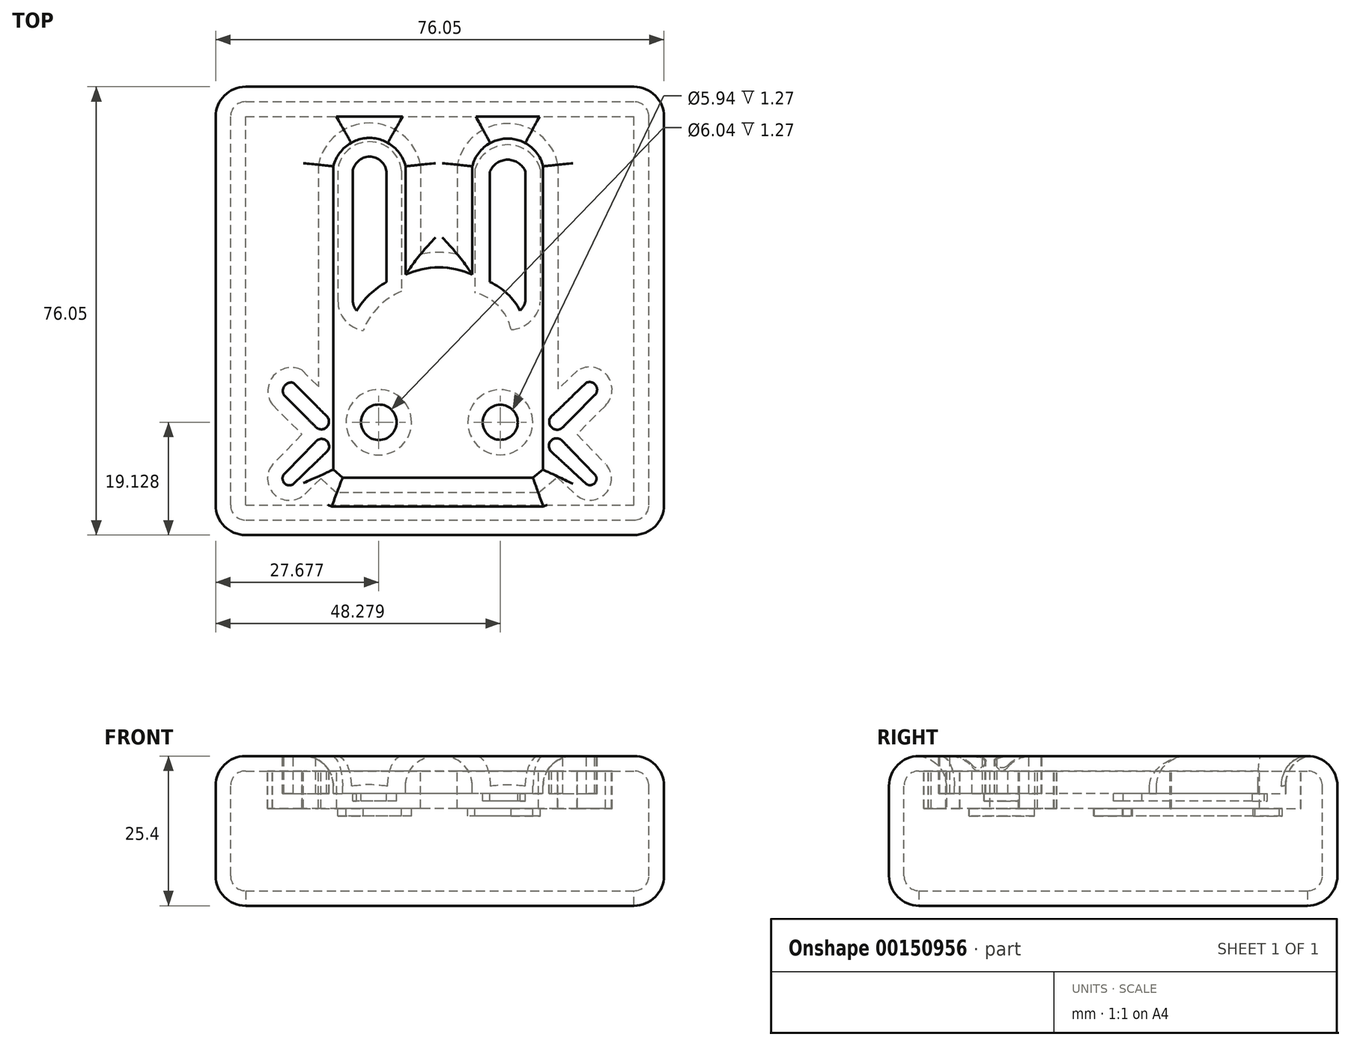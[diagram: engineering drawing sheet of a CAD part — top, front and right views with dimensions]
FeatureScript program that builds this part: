
annotation { "Feature Type Name" : "Feature", "Feature Type Description" : "" }
export const myFeature = defineFeature(function(context is Context, id is Id, definition is map)
    precondition{}
    {
        {
            var Q0;
            Q0=qCreatedBy(makeId("Top.planeOp"),FACE);
            var sketch = newSketch(context, id + "F0", { "sketchPlane" : qUnion([Q0])});
            skLineSegment(sketch, "E0.bottom", {"start": v(0, 0) * mm, "end": v(76.05, 0) * mm});
            skLineSegment(sketch, "E0.top", {"start": v(0, 76.05) * mm, "end": v(76.05, 76.05) * mm});
            skLineSegment(sketch, "E0.left", {"start": v(0, 0) * mm, "end": v(0, 76.05) * mm});
            skLineSegment(sketch, "E0.right", {"start": v(76.05, 0) * mm, "end": v(76.05, 76.05) * mm});
            skSolve(sketch);
        }
        {
            var Q0;
            Q0 = qSketchRegion(id + "F0", true);
            extrude(context, id + "F1", {"entities" : qUnion([Q0]), "depth" : 25.4 * mm});
        }
        {
            var Q0;
            Q0=makeQuery(id+"F1.opExtrude","CAP_FACE",FACE,{"disambiguationData":[OSD([sQuery(id+"F0.wireOp",EDGE,"E0.bottom"),sQuery(id+"F0.wireOp",EDGE,"E0.top"),sQuery(id+"F0.wireOp",EDGE,"E0.left"),sQuery(id+"F0.wireOp",EDGE,"E0.right")])],"isStart":false});
            var sketch = newSketch(context, id + "F2", { "sketchPlane" : qUnion([Q0])});
            skPoint(sketch, "E1", {"position": v(11.59, 23.74) * mm});
            skPoint(sketch, "E2", {"position": v(11.59, 10.3) * mm});
            skPoint(sketch, "E3", {"position": v(13.2, 8.63) * mm});
            skPoint(sketch, "E4", {"position": v(13.2, 25.84) * mm});
            skPoint(sketch, "E5", {"position": v(64.31, 23.74) * mm});
            skPoint(sketch, "E6", {"position": v(64.31, 10.3) * mm});
            skPoint(sketch, "E7", {"position": v(62.9, 25.84) * mm});
            skPoint(sketch, "E8", {"position": v(62.9, 8.63) * mm});
            skPoint(sketch, "E9", {"position": v(17.01, 15.85) * mm});
            skPoint(sketch, "E10", {"position": v(17.01, 18.3) * mm});
            skPoint(sketch, "E11", {"position": v(18.82, 20.17) * mm});
            skPoint(sketch, "E12", {"position": v(18.82, 14.1) * mm});
            skPoint(sketch, "E13", {"position": v(58.92, 15.85) * mm});
            skPoint(sketch, "E14", {"position": v(58.92, 18.3) * mm});
            skPoint(sketch, "E15", {"position": v(57, 20.17) * mm});
            skPoint(sketch, "E16", {"position": v(57, 14.1) * mm});
            skPoint(sketch, "E17", {"position": v(27.68, 19.13) * mm});
            skPoint(sketch, "E18", {"position": v(48.28, 19.13) * mm});
            skCircle(sketch, "E19", {"center": v(27.68, 19.13) * mm, "radius": 3.02 * mm});
            skCircle(sketch, "E20", {"center": v(48.28, 19.13) * mm, "radius": 2.97 * mm});
            skArc(sketch, "E21", {"start": v(13.2, 25.84) * mm, "mid": v(11.7, 25.31) * mm, "end": v(11.59, 23.74) * mm});
            skArc(sketch, "E22", {"start": v(17.01, 18.3) * mm, "mid": v(18.86, 18.32) * mm, "end": v(18.82, 20.17) * mm});
            skArc(sketch, "E23", {"start": v(18.82, 14.1) * mm, "mid": v(18.86, 15.95) * mm, "end": v(17.01, 15.85) * mm});
            skArc(sketch, "E24", {"start": v(11.59, 10.3) * mm, "mid": v(11.68, 8.78) * mm, "end": v(13.2, 8.63) * mm});
            skArc(sketch, "E25", {"start": v(57, 20.17) * mm, "mid": v(57, 18.25) * mm, "end": v(58.92, 18.3) * mm});
            skArc(sketch, "E26", {"start": v(64.31, 23.74) * mm, "mid": v(64.5, 25.38) * mm, "end": v(62.9, 25.84) * mm});
            skArc(sketch, "E27", {"start": v(58.92, 15.85) * mm, "mid": v(56.96, 16.07) * mm, "end": v(57, 14.1) * mm});
            skArc(sketch, "E28", {"start": v(62.9, 8.63) * mm, "mid": v(64.34, 8.85) * mm, "end": v(64.31, 10.3) * mm});
            skLineSegment(sketch, "E29", {"start": v(13.2, 25.84) * mm, "end": v(18.82, 20.17) * mm});
            skLineSegment(sketch, "E30", {"start": v(11.59, 23.74) * mm, "end": v(17.01, 18.3) * mm});
            skLineSegment(sketch, "E31", {"start": v(17.01, 15.85) * mm, "end": v(11.59, 10.3) * mm});
            skLineSegment(sketch, "E32", {"start": v(18.82, 14.1) * mm, "end": v(13.2, 8.63) * mm});
            skLineSegment(sketch, "E33", {"start": v(57, 14.1) * mm, "end": v(62.9, 8.63) * mm});
            skLineSegment(sketch, "E34", {"start": v(58.92, 15.85) * mm, "end": v(64.31, 10.3) * mm});
            skLineSegment(sketch, "E35", {"start": v(64.31, 23.74) * mm, "end": v(58.92, 18.3) * mm});
            skLineSegment(sketch, "E36", {"start": v(62.9, 25.84) * mm, "end": v(57, 20.17) * mm});
            skPoint(sketch, "E37", {"position": v(23.24, 61.64) * mm});
            skPoint(sketch, "E38", {"position": v(29, 61.64) * mm});
            skPoint(sketch, "E39", {"position": v(46.53, 61.64) * mm});
            skPoint(sketch, "E40", {"position": v(52.56, 61.64) * mm});
            skPoint(sketch, "E41", {"position": v(52.56, 39.74) * mm});
            skPoint(sketch, "E42", {"position": v(51.63, 38.07) * mm});
            skPoint(sketch, "E43", {"position": v(23.89, 38.07) * mm});
            skPoint(sketch, "E44", {"position": v(23.28, 39.74) * mm});
            skPoint(sketch, "E45", {"position": v(29, 42.91) * mm});
            skPoint(sketch, "E46", {"position": v(46.53, 42.91) * mm});
            skArc(sketch, "E47", {"start": v(29, 61.64) * mm, "mid": v(26.12, 64.18) * mm, "end": v(23.24, 61.64) * mm});
            skArc(sketch, "E48", {"start": v(52.56, 61.64) * mm, "mid": v(49.54, 63.67) * mm, "end": v(46.53, 61.64) * mm});
            skArc(sketch, "E49", {"start": v(51.63, 38.07) * mm, "mid": v(49.5, 40.93) * mm, "end": v(46.53, 42.91) * mm});
            skArc(sketch, "E50", {"start": v(29, 42.91) * mm, "mid": v(26.14, 40.81) * mm, "end": v(23.89, 38.07) * mm});
            skArc(sketch, "E51", {"start": v(23.28, 39.74) * mm, "mid": v(23.43, 38.85) * mm, "end": v(23.89, 38.07) * mm});
            skArc(sketch, "E52", {"start": v(51.63, 38.07) * mm, "mid": v(52.24, 38.82) * mm, "end": v(52.56, 39.74) * mm});
            skLineSegment(sketch, "E53", {"start": v(23.24, 61.64) * mm, "end": v(23.28, 39.74) * mm});
            skLineSegment(sketch, "E54", {"start": v(29, 61.64) * mm, "end": v(29, 42.91) * mm});
            skLineSegment(sketch, "E55", {"start": v(46.53, 61.64) * mm, "end": v(46.53, 42.91) * mm});
            skLineSegment(sketch, "E56", {"start": v(52.56, 61.64) * mm, "end": v(52.56, 39.74) * mm});
            skPoint(sketch, "E57", {"position": v(19.97, 62.55) * mm});
            skPoint(sketch, "E58", {"position": v(32.22, 62.55) * mm});
            skPoint(sketch, "E59", {"position": v(43.54, 62.55) * mm});
            skPoint(sketch, "E60", {"position": v(55.55, 62.55) * mm});
            skPoint(sketch, "E61", {"position": v(19.97, 11.1) * mm});
            skPoint(sketch, "E62", {"position": v(55.55, 11.1) * mm});
            skPoint(sketch, "E63", {"position": v(53.84, 9.7) * mm});
            skPoint(sketch, "E64", {"position": v(21.54, 9.7) * mm});
            skArc(sketch, "E65", {"start": v(32.22, 62.55) * mm, "mid": v(26.1, 67.36) * mm, "end": v(19.97, 62.55) * mm});
            skArc(sketch, "E66", {"start": v(55.55, 62.55) * mm, "mid": v(49.54, 67.26) * mm, "end": v(43.54, 62.55) * mm});
            skPoint(sketch, "E67", {"position": v(32.22, 44.18) * mm});
            skPoint(sketch, "E68", {"position": v(43.54, 44.18) * mm});
            skArc(sketch, "E69", {"start": v(43.54, 44.18) * mm, "mid": v(37.88, 45.4) * mm, "end": v(32.22, 44.18) * mm});
            skLineSegment(sketch, "E70", {"start": v(19.97, 62.55) * mm, "end": v(19.97, 11.1) * mm});
            skLineSegment(sketch, "E71", {"start": v(19.97, 11.1) * mm, "end": v(21.54, 9.7) * mm});
            skLineSegment(sketch, "E72", {"start": v(53.84, 9.7) * mm, "end": v(55.55, 11.1) * mm});
            skLineSegment(sketch, "E73", {"start": v(53.84, 9.7) * mm, "end": v(21.54, 9.7) * mm});
            skLineSegment(sketch, "E74", {"start": v(55.55, 62.55) * mm, "end": v(55.55, 11.1) * mm});
            skLineSegment(sketch, "E75", {"start": v(43.54, 62.55) * mm, "end": v(43.54, 44.18) * mm});
            skLineSegment(sketch, "E76", {"start": v(32.22, 62.55) * mm, "end": v(32.22, 44.18) * mm});
            skSolve(sketch);
        }
        {
            var Q0;
            Q0 = qSketchRegion(id + "F2", true);
            extrude(context, id + "F3", {"entities" : qUnion([Q0]), "operationType" : NewBodyOperationType.REMOVE, "oppositeDirection" : true, "depth" : 6.35 * mm});
        }
        {
            var Q0;
            Q0=makeQuery(id+"F3.boolean.opBoolean","SPLIT",FACE,{"disambiguationData":[TD([makeQuery(id+"F3.opExtrude","SWEPT_FACE",FACE,{"disambiguationData":[OSD([sQuery(id+"F2.wireOp",EDGE,"E47")])]})])],"derivedFrom":makeQuery(id+"F1.opExtrude","CAP_FACE",FACE,{"disambiguationData":[OSD([sQuery(id+"F0.wireOp",EDGE,"E0.bottom"),sQuery(id+"F0.wireOp",EDGE,"E0.top"),sQuery(id+"F0.wireOp",EDGE,"E0.left"),sQuery(id+"F0.wireOp",EDGE,"E0.right")])],"isStart":false})});
            var Q1;
            Q1=makeQuery(id+"F3.boolean.opBoolean","SPLIT",FACE,{"disambiguationData":[TD([makeQuery(id+"F3.opExtrude","SWEPT_FACE",FACE,{"disambiguationData":[OSD([sQuery(id+"F2.wireOp",EDGE,"E48")])]})])],"derivedFrom":makeQuery(id+"F1.opExtrude","CAP_FACE",FACE,{"disambiguationData":[OSD([sQuery(id+"F0.wireOp",EDGE,"E0.bottom"),sQuery(id+"F0.wireOp",EDGE,"E0.top"),sQuery(id+"F0.wireOp",EDGE,"E0.left"),sQuery(id+"F0.wireOp",EDGE,"E0.right")])],"isStart":false})});
            var Q2;
            Q2=makeQuery(id+"F3.boolean.opBoolean","SPLIT",FACE,{"disambiguationData":[TD([makeQuery(id+"F3.opExtrude","SWEPT_FACE",FACE,{"disambiguationData":[OSD([sQuery(id+"F2.wireOp",EDGE,"E20")])]})])],"derivedFrom":makeQuery(id+"F1.opExtrude","CAP_FACE",FACE,{"disambiguationData":[OSD([sQuery(id+"F0.wireOp",EDGE,"E0.bottom"),sQuery(id+"F0.wireOp",EDGE,"E0.top"),sQuery(id+"F0.wireOp",EDGE,"E0.left"),sQuery(id+"F0.wireOp",EDGE,"E0.right")])],"isStart":false})});
            var Q3;
            Q3=makeQuery(id+"F3.boolean.opBoolean","SPLIT",FACE,{"disambiguationData":[TD([makeQuery(id+"F3.opExtrude","SWEPT_FACE",FACE,{"disambiguationData":[OSD([sQuery(id+"F2.wireOp",EDGE,"E19")])]})])],"derivedFrom":makeQuery(id+"F1.opExtrude","CAP_FACE",FACE,{"disambiguationData":[OSD([sQuery(id+"F0.wireOp",EDGE,"E0.bottom"),sQuery(id+"F0.wireOp",EDGE,"E0.top"),sQuery(id+"F0.wireOp",EDGE,"E0.left"),sQuery(id+"F0.wireOp",EDGE,"E0.right")])],"isStart":false})});
            extrude(context, id + "F4", {"entities" : qUnion([Q0, Q1, Q2, Q3]), "operationType" : NewBodyOperationType.REMOVE, "oppositeDirection" : true, "depth" : 7.62 * mm});
        }
        {
            var Q0;
            Q0=makeQuery(id+"F1.opExtrude","CAP_EDGE",EDGE,{"disambiguationData":[OSD([sQuery(id+"F0.wireOp",EDGE,"E0.top")])],"isStart":false});
            var Q1;
            Q1=makeQuery(id+"F1.opExtrude","CAP_EDGE",EDGE,{"disambiguationData":[OSD([sQuery(id+"F0.wireOp",EDGE,"E0.left")])],"isStart":false});
            var Q2;
            Q2=makeQuery(id+"F1.opExtrude","CAP_EDGE",EDGE,{"disambiguationData":[OSD([sQuery(id+"F0.wireOp",EDGE,"E0.bottom")])],"isStart":false});
            var Q3;
            Q3=makeQuery(id+"F1.opExtrude","CAP_EDGE",EDGE,{"disambiguationData":[OSD([sQuery(id+"F0.wireOp",EDGE,"E0.right")])],"isStart":false});
            var Q4;
            Q4=makeQuery(id+"F1.opExtrude","CAP_EDGE",EDGE,{"disambiguationData":[OSD([sQuery(id+"F0.wireOp",EDGE,"E0.right")])],"isStart":true});
            var Q5;
            Q5=makeQuery(id+"F1.opExtrude","SWEPT_FACE",FACE,{"disambiguationData":[OSD([sQuery(id+"F0.wireOp",EDGE,"E0.right")])]});
            var Q6;
            Q6=makeQuery(id+"F1.opExtrude","CAP_EDGE",EDGE,{"disambiguationData":[OSD([sQuery(id+"F0.wireOp",EDGE,"E0.bottom")])],"isStart":true});
            var Q7;
            Q7=makeQuery(id+"F1.opExtrude","SWEPT_EDGE",EDGE,{"disambiguationData":[OSD([sQuery(id+"F0.wireOp",EDGE,"E0.bottom"),sQuery(id+"F0.wireOp",EDGE,"E0.left")])]});
            var Q8;
            Q8=makeQuery(id+"F1.opExtrude","CAP_EDGE",EDGE,{"disambiguationData":[OSD([sQuery(id+"F0.wireOp",EDGE,"E0.left")])],"isStart":true});
            var Q9;
            Q9=makeQuery(id+"F1.opExtrude","SWEPT_FACE",FACE,{"disambiguationData":[OSD([sQuery(id+"F0.wireOp",EDGE,"E0.top")])]});
            fillet(context, id + "F5", {"entities" : qUnion([Q0, Q1, Q2, Q3, Q4, Q5, Q6, Q7, Q8, Q9]), "radius" : 5.08 * mm, "tangentPropagation" : true, "allowEdgeOverflow" : false});
        }
        {
            var Q0;
            Q0=makeQuery(id+"F1.opExtrude","CAP_FACE",FACE,{"disambiguationData":[OSD([sQuery(id+"F0.wireOp",EDGE,"E0.bottom"),sQuery(id+"F0.wireOp",EDGE,"E0.top"),sQuery(id+"F0.wireOp",EDGE,"E0.left"),sQuery(id+"F0.wireOp",EDGE,"E0.right")])],"isStart":true});
            shell(context, id + "F6", {"entities" : qUnion([Q0]), "thickness" : 2.54 * mm});
        }
        {
            var Q0;
            Q0=makeQuery(id+"F3.boolean.opBoolean","COPY",EDGE,{"derivedFrom":makeQuery(id+"F3.opExtrude","CAP_EDGE",EDGE,{"disambiguationData":[OSD([sQuery(id+"F2.wireOp",EDGE,"E65")])],"isStart":true})});
            var Q1;
            Q1=makeQuery(id+"F3.boolean.opBoolean","COPY",EDGE,{"derivedFrom":makeQuery(id+"F3.opExtrude","CAP_EDGE",EDGE,{"disambiguationData":[OSD([sQuery(id+"F2.wireOp",EDGE,"E76")])],"isStart":true})});
            var Q2;
            Q2=makeQuery(id+"F3.boolean.opBoolean","COPY",EDGE,{"derivedFrom":makeQuery(id+"F3.opExtrude","CAP_EDGE",EDGE,{"disambiguationData":[OSD([sQuery(id+"F2.wireOp",EDGE,"E69")])],"isStart":true})});
            var Q3;
            Q3=makeQuery(id+"F3.boolean.opBoolean","COPY",EDGE,{"derivedFrom":makeQuery(id+"F3.opExtrude","CAP_EDGE",EDGE,{"disambiguationData":[OSD([sQuery(id+"F2.wireOp",EDGE,"E75")])],"isStart":true})});
            var Q4;
            Q4=makeQuery(id+"F3.boolean.opBoolean","COPY",EDGE,{"derivedFrom":makeQuery(id+"F3.opExtrude","CAP_EDGE",EDGE,{"disambiguationData":[OSD([sQuery(id+"F2.wireOp",EDGE,"E66")])],"isStart":true})});
            var Q5;
            Q5=makeQuery(id+"F3.boolean.opBoolean","COPY",EDGE,{"derivedFrom":makeQuery(id+"F3.opExtrude","CAP_EDGE",EDGE,{"disambiguationData":[OSD([sQuery(id+"F2.wireOp",EDGE,"E74")])],"isStart":true})});
            var Q6;
            Q6=makeQuery(id+"F3.boolean.opBoolean","COPY",EDGE,{"derivedFrom":makeQuery(id+"F3.opExtrude","CAP_EDGE",EDGE,{"disambiguationData":[OSD([sQuery(id+"F2.wireOp",EDGE,"E70")])],"isStart":true})});
            var Q7;
            Q7=makeQuery(id+"F3.boolean.opBoolean","COPY",EDGE,{"derivedFrom":makeQuery(id+"F3.opExtrude","CAP_EDGE",EDGE,{"disambiguationData":[OSD([sQuery(id+"F2.wireOp",EDGE,"E71")])],"isStart":true})});
            var Q8;
            Q8=makeQuery(id+"F3.boolean.opBoolean","COPY",EDGE,{"derivedFrom":makeQuery(id+"F3.opExtrude","CAP_EDGE",EDGE,{"disambiguationData":[OSD([sQuery(id+"F2.wireOp",EDGE,"E73")])],"isStart":true})});
            var Q9;
            Q9=makeQuery(id+"F3.boolean.opBoolean","COPY",EDGE,{"derivedFrom":makeQuery(id+"F3.opExtrude","CAP_EDGE",EDGE,{"disambiguationData":[OSD([sQuery(id+"F2.wireOp",EDGE,"E72")])],"isStart":true})});
            fillet(context, id + "F7", {"entities" : qUnion([Q0, Q1, Q2, Q3, Q4, Q5, Q6, Q7, Q8, Q9]), "radius" : 5.08 * mm, "tangentPropagation" : true, "allowEdgeOverflow" : false});
        }
    });
